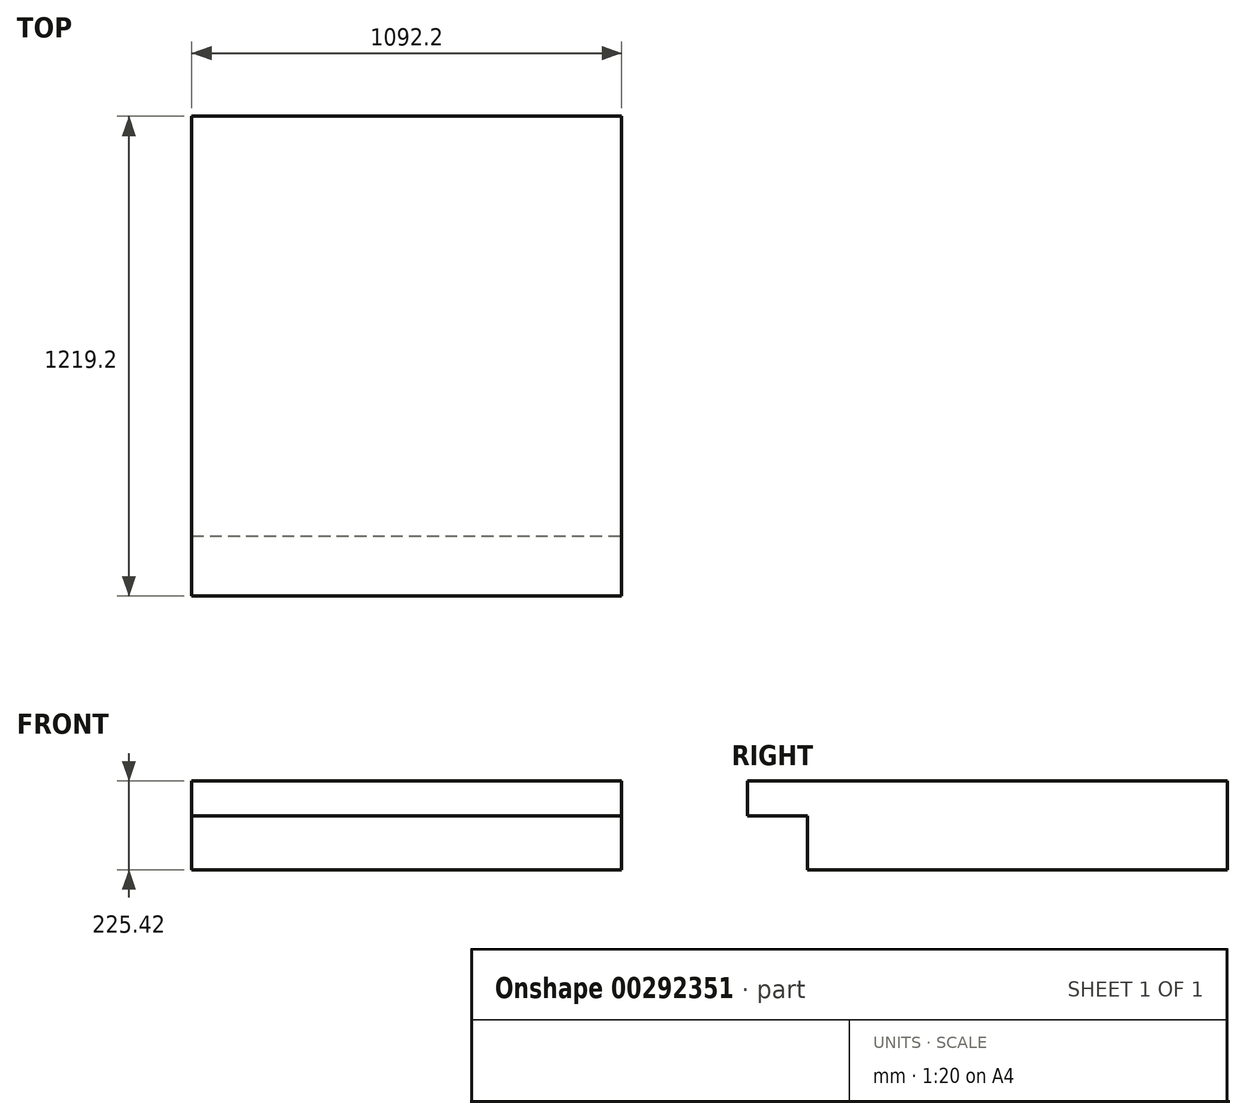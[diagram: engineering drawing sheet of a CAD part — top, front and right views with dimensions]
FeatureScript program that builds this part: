
annotation { "Feature Type Name" : "Feature", "Feature Type Description" : "" }
export const myFeature = defineFeature(function(context is Context, id is Id, definition is map)
    precondition{}
    {
        {
            var Q0;
            Q0=qCreatedBy(makeId("Top.planeOp"),FACE);
            var sketch = newSketch(context, id + "F0", { "sketchPlane" : qUnion([Q0])});
            skLineSegment(sketch, "E0.bottom", {"start": v(546.1, -1219.2) * mm, "end": v(-546.1, -1219.2) * mm});
            skLineSegment(sketch, "E0.top", {"start": v(546.1, 0) * mm, "end": v(-546.1, 0) * mm});
            skLineSegment(sketch, "E0.left", {"start": v(546.1, 0) * mm, "end": v(546.1, -1219.2) * mm});
            skLineSegment(sketch, "E0.right", {"start": v(-546.1, 0) * mm, "end": v(-546.1, -1219.2) * mm});
            skPoint(sketch, "E0.middle", {"position": v(0, -609.6) * mm});
            skSolve(sketch);
        }
        {
            var Q0;
            Q0=makeQuery(id+"F0.imprint","IMPRINT",FACE,{"disambiguationData":[TD([[makeQuery(id+"F0.imprint","IMPRINT",EDGE,{"derivedFrom":sQuery(id+"F0.wireOp",EDGE,"E0.bottom")}),-1.0]])]});
            extrude(context, id + "F1", {"entities" : qUnion([Q0]), "oppositeDirection" : true, "depth" : 225.42 * mm, "offsetDistance" : 25.4 * mm});
        }
        {
            var Q0;
            Q0=makeQuery(id+"F1.opExtrude","SWEPT_FACE",FACE,{"disambiguationData":[OSD([sQuery(id+"F0.wireOp",EDGE,"E0.left")])]});
            var sketch = newSketch(context, id + "F2", { "sketchPlane" : qUnion([Q0])});
            skLineSegment(sketch, "E1.bottom", {"start": v(-1219.2, -225.43) * mm, "end": v(-1066.8, -225.43) * mm});
            skLineSegment(sketch, "E1.top", {"start": v(-1219.2, -88.9) * mm, "end": v(-1066.8, -88.9) * mm});
            skLineSegment(sketch, "E1.left", {"start": v(-1219.2, -225.43) * mm, "end": v(-1219.2, -88.9) * mm});
            skLineSegment(sketch, "E1.right", {"start": v(-1066.8, -225.43) * mm, "end": v(-1066.8, -88.9) * mm});
            skSolve(sketch);
        }
        {
            var Q0;
            Q0 = qSketchRegion(id + "F2", true);
            extrude(context, id + "F3", {"entities" : qUnion([Q0]), "operationType" : NewBodyOperationType.REMOVE, "endBound" : BoundingType.UP_TO_NEXT, "oppositeDirection" : true, "depth" : 25.4 * mm, "offsetDistance" : 25.4 * mm});
        }
    });
